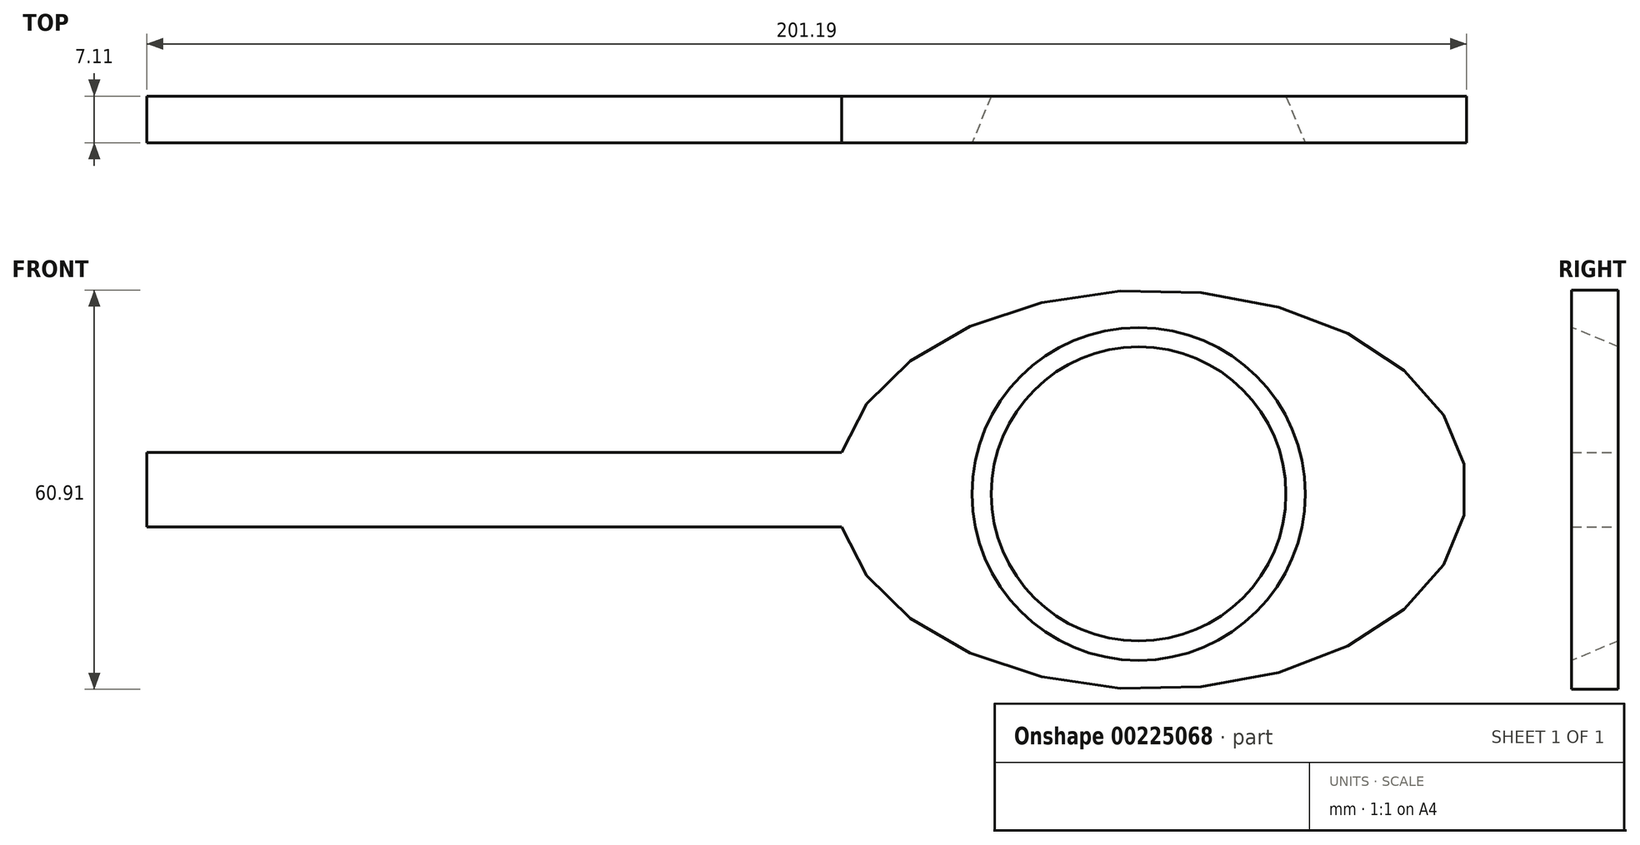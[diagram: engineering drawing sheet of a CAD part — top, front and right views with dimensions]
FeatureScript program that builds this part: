
annotation { "Feature Type Name" : "Feature", "Feature Type Description" : "" }
export const myFeature = defineFeature(function(context is Context, id is Id, definition is map)
    precondition{}
    {
        {
            var Q0;
            Q0=qCreatedBy(makeId("Front.planeOp"),FACE);
            var sketch = newSketch(context, id + "F0", { "sketchPlane" : qUnion([Q0])});
            skLineSegment(sketch, "E0.bottom", {"start": v(-19.82, 17.66) * mm, "end": v(-172.94, 17.66) * mm});
            skLineSegment(sketch, "E0.top", {"start": v(-19.82, 6.27) * mm, "end": v(-172.94, 6.27) * mm});
            skLineSegment(sketch, "E0.left", {"start": v(-19.82, 17.66) * mm, "end": v(-19.82, 6.27) * mm});
            skLineSegment(sketch, "E0.right", {"start": v(-172.94, 17.66) * mm, "end": v(-172.94, 6.27) * mm});
            skPoint(sketch, "E0.middle", {"position": v(-96.38, 11.96) * mm});
            skEllipse(sketch, "E1", {"center": v(-19.82, 11.96) * mm, "majorRadius": 48.08 * mm, "minorRadius": 30.45 * mm, "majorAxis": v(1, 0)});
            skSolve(sketch);
        }
        {
            var Q0;
            Q0 = qSketchRegion(id + "F0", true);
            extrude(context, id + "F1", {"entities" : qUnion([Q0]), "depth" : 7.11 * mm});
        }
        {
            var Q0;
            Q0=makeQuery(id+"F1.opExtrude","CAP_FACE",FACE,{"disambiguationData":[OSD([sQuery(id+"F0.wireOp",EDGE,"E0.bottom"),sQuery(id+"F0.wireOp",EDGE,"E0.top"),sQuery(id+"F0.wireOp",EDGE,"E0.right"),sQuery(id+"F0.wireOp",EDGE,"E1")])],"isStart":false});
            var sketch = newSketch(context, id + "F2", { "sketchPlane" : qUnion([Q0])});
            skEllipse(sketch, "E2", {"center": v(-21.76, 11.33) * mm, "majorRadius": 40.8 * mm, "minorRadius": 26.56 * mm, "majorAxis": v(1, 0)});
            skSolve(sketch);
        }
        {
            var Q0;
            Q0=sQuery(id+"F2.wireOp",VERTEX,"E2.center");
            var Q1;
            Q1=makeQuery(id+"F1.opExtrude","SWEPT_BODY",BODY,{"disambiguationData":[OSD([sQuery(id+"F0.wireOp",EDGE,"E0.bottom"),sQuery(id+"F0.wireOp",EDGE,"E0.top"),sQuery(id+"F0.wireOp",EDGE,"E0.right"),sQuery(id+"F0.wireOp",EDGE,"E1")])]});
            hole(context, id + "F3", {"style" : HoleStyle.C_SINK, "endStyle" : HoleEndStyle.THROUGH, "holeDiameter" : 12.7 * mm, "cSinkDiameter" : 50.8 * mm, "cSinkAngle" : 45 * degree, "locations" : qUnion([Q0]), "scope" : qUnion([Q1]), "isTappedThrough" : true});
        }
    });
